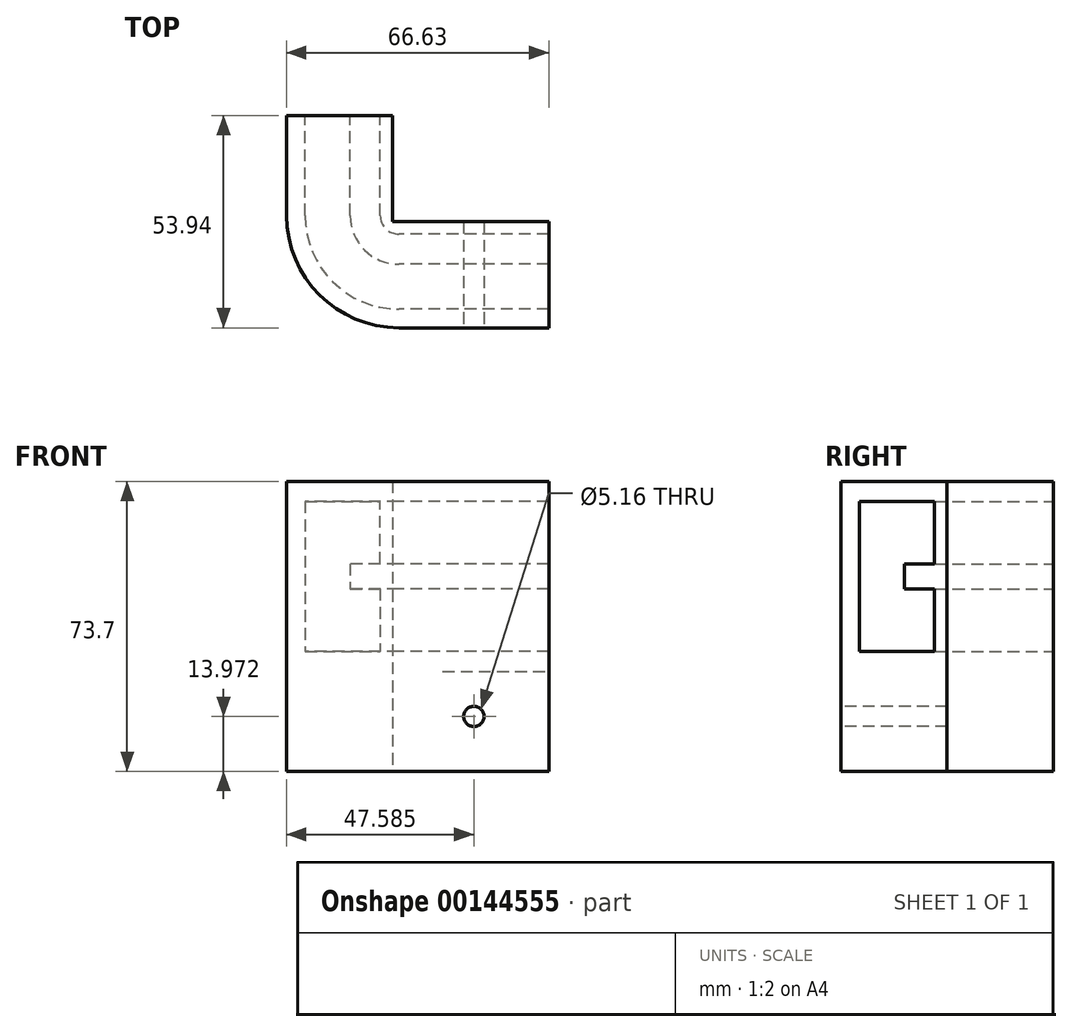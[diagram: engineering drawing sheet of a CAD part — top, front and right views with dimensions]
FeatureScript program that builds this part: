
annotation { "Feature Type Name" : "Feature", "Feature Type Description" : "" }
export const myFeature = defineFeature(function(context is Context, id is Id, definition is map)
    precondition{}
    {
        {
            var Q0;
            Q0=qCreatedBy(makeId("Front.planeOp"),FACE);
            var sketch = newSketch(context, id + "F0", { "sketchPlane" : qUnion([Q0])});
            skLineSegment(sketch, "E0.bottom", {"start": v(-12.7, 18.7) * mm, "end": v(6.35, 18.7) * mm});
            skLineSegment(sketch, "E0.top", {"start": v(-12.7, -19.4) * mm, "end": v(6.35, -19.4) * mm});
            skLineSegment(sketch, "E0.left", {"start": v(-12.7, 18.7) * mm, "end": v(-12.7, -19.4) * mm});
            skLineSegment(sketch, "E1", {"start": v(6.35, -3.53) * mm, "end": v(6.35, -19.4) * mm});
            skLineSegment(sketch, "E2", {"start": v(6.35, 2.82) * mm, "end": v(6.35, 18.7) * mm});
            skLineSegment(sketch, "E3", {"start": v(6.35, 2.82) * mm, "end": v(-1.27, 2.82) * mm});
            skLineSegment(sketch, "E4.bottom", {"start": v(-1.27, 2.82) * mm, "end": v(6.35, 2.82) * mm});
            skLineSegment(sketch, "E4.top", {"start": v(-1.27, -3.53) * mm, "end": v(6.35, -3.53) * mm});
            skLineSegment(sketch, "E4.left", {"start": v(-1.27, 2.82) * mm, "end": v(-1.27, -3.53) * mm});
            skLineSegment(sketch, "E5.bottom", {"start": v(-17.44, 23.8) * mm, "end": v(11.1, 23.8) * mm});
            skLineSegment(sketch, "E5.top", {"start": v(-17.44, -24.5) * mm, "end": v(11.1, -24.5) * mm});
            skLineSegment(sketch, "E5.left", {"start": v(-17.44, 23.8) * mm, "end": v(-17.44, -24.5) * mm});
            skLineSegment(sketch, "E5.right", {"start": v(11.1, 23.8) * mm, "end": v(11.1, -24.5) * mm});
            skLineSegment(sketch, "E6", {"start": v(-12.7, 18.7) * mm, "end": v(-17.44, 23.8) * mm, "construction": true});
            skLineSegment(sketch, "E7", {"start": v(6.35, 18.7) * mm, "end": v(11.1, 23.8) * mm, "construction": true});
            skLineSegment(sketch, "E8", {"start": v(6.35, -19.4) * mm, "end": v(11.1, -24.5) * mm, "construction": true});
            skLineSegment(sketch, "E9", {"start": v(-17.44, -24.5) * mm, "end": v(-12.7, -19.4) * mm, "construction": true});
            skSolve(sketch);
        }
        {
            var Q0;
            Q0=makeQuery(id+"F0.imprint","IMPRINT",FACE,{"disambiguationData":[TD([[makeQuery(id+"F0.imprint","IMPRINT",EDGE,{"derivedFrom":sQuery(id+"F0.wireOp",EDGE,"E0.bottom")}),1.0]])]});
            var Q1;
            Q1=sQuery(id+"F0.wireOp",EDGE,"E8");
            var Q2;
            Q2=sQuery(id+"F0.wireOp",EDGE,"E9");
            var Q3;
            Q3=sQuery(id+"F0.wireOp",EDGE,"E6");
            var Q4;
            Q4=sQuery(id+"F0.wireOp",EDGE,"E7");
            extrude(context, id + "F1", {"entities" : qUnion([Q0]), "surfaceEntities" : qUnion([Q1, Q2, Q3, Q4]), "depth" : 25.4 * mm});
        }
        {
            var Q0;
            Q0=makeQuery(id+"F1.opExtrude","CAP_FACE",FACE,{"disambiguationData":[OSD([sQuery(id+"F0.wireOp",EDGE,"E0.bottom"),sQuery(id+"F0.wireOp",EDGE,"E0.top"),sQuery(id+"F0.wireOp",EDGE,"E0.left"),sQuery(id+"F0.wireOp",EDGE,"E1"),sQuery(id+"F0.wireOp",EDGE,"E2"),sQuery(id+"F0.wireOp",EDGE,"E4.bottom"),sQuery(id+"F0.wireOp",EDGE,"E4.top"),sQuery(id+"F0.wireOp",EDGE,"E4.left"),sQuery(id+"F0.wireOp",EDGE,"E5.bottom"),sQuery(id+"F0.wireOp",EDGE,"E5.top"),sQuery(id+"F0.wireOp",EDGE,"E5.left"),sQuery(id+"F0.wireOp",EDGE,"E5.right")])],"isStart":false});
            var Q1;
            Q1=makeQuery(id+"F1.opExtrude","CAP_EDGE",EDGE,{"disambiguationData":[OSD([sQuery(id+"F0.wireOp",EDGE,"E5.right")])],"isStart":false});
            revolve(context, id + "F2", {"operationType" : NewBodyOperationType.ADD, "entities" : qUnion([Q0]), "axis" : qUnion([Q1]), "revolveType" : RevolveType.ONE_DIRECTION, "oppositeDirection" : true, "angle" : 90 * degree});
        }
        {
            var Q0;
            {var subQ0=sQuery(id+"F0.wireOp",EDGE,"E5.right");Q0=makeQuery(id+"F2.boolean.opBoolean","MERGE",FACE,{"derivedFrom":[makeQuery(id+"F1.opExtrude","SWEPT_FACE",FACE,{"disambiguationData":[OSD([subQ0])]}),makeQuery(id+"F2.opRevolve","CAP_FACE",FACE,{"disambiguationData":[OSD([sQuery(id+"F0.wireOp",EDGE,"E0.bottom"),sQuery(id+"F0.wireOp",EDGE,"E0.top"),sQuery(id+"F0.wireOp",EDGE,"E0.left"),sQuery(id+"F0.wireOp",EDGE,"E1"),sQuery(id+"F0.wireOp",EDGE,"E2"),sQuery(id+"F0.wireOp",EDGE,"E4.bottom"),sQuery(id+"F0.wireOp",EDGE,"E4.top"),sQuery(id+"F0.wireOp",EDGE,"E4.left"),sQuery(id+"F0.wireOp",EDGE,"E5.bottom"),sQuery(id+"F0.wireOp",EDGE,"E5.top"),sQuery(id+"F0.wireOp",EDGE,"E5.left"),subQ0])],"isStart":false})]});}
            extrude(context, id + "F3", {"entities" : qUnion([Q0]), "operationType" : NewBodyOperationType.ADD, "depth" : 38.1 * mm, "offsetDistance" : 25.4 * mm});
        }
        {
            var Q0;
            {var subQ0=sQuery(id+"F0.wireOp",EDGE,"E5.top");Q0=makeQuery(id+"F3.boolean.opBoolean","MERGE",FACE,{"derivedFrom":[makeQuery(id+"F2.boolean.opBoolean","MERGE",FACE,{"derivedFrom":[makeQuery(id+"F1.opExtrude","SWEPT_FACE",FACE,{"disambiguationData":[OSD([subQ0])]}),makeQuery(id+"F2.opRevolve","SWEPT_FACE",FACE,{"disambiguationData":[OSD([subQ0])]})]}),makeQuery(id+"F3.opExtrude","SWEPT_FACE",FACE,{"disambiguationData":[OSD([subQ0,sQuery(id+"F0.wireOp",EDGE,"E5.right")])]})]});}
            var sketch = newSketch(context, id + "F4", { "sketchPlane" : qUnion([Q0])});
            skLineSegment(sketch, "E10.bottom", {"start": v(22.23, 0) * mm, "end": v(49.2, 0) * mm});
            skLineSegment(sketch, "E10.top", {"start": v(22.23, 26.97) * mm, "end": v(49.2, 26.97) * mm});
            skLineSegment(sketch, "E10.left", {"start": v(22.23, 0) * mm, "end": v(22.23, 26.97) * mm});
            skLineSegment(sketch, "E10.right", {"start": v(49.2, 0) * mm, "end": v(49.2, 26.97) * mm});
            skSolve(sketch);
        }
        {
            var Q0;
            Q0 = qSketchRegion(id + "F4", true);
            extrude(context, id + "F5", {"entities" : qUnion([Q0]), "operationType" : NewBodyOperationType.REMOVE, "endBound" : BoundingType.SYMMETRIC, "oppositeDirection" : true, "depth" : 100.3 * mm});
        }
        {
            var Q0;
            {var subQ0=sQuery(id+"F0.wireOp",EDGE,"E5.top");Q0=makeQuery(id+"F3.boolean.opBoolean","MERGE",FACE,{"derivedFrom":[makeQuery(id+"F2.boolean.opBoolean","MERGE",FACE,{"derivedFrom":[makeQuery(id+"F1.opExtrude","SWEPT_FACE",FACE,{"disambiguationData":[OSD([subQ0])]}),makeQuery(id+"F2.opRevolve","SWEPT_FACE",FACE,{"disambiguationData":[OSD([subQ0])]})]}),makeQuery(id+"F3.opExtrude","SWEPT_FACE",FACE,{"disambiguationData":[OSD([subQ0,sQuery(id+"F0.wireOp",EDGE,"E5.right")])]})]});}
            var sketch = newSketch(context, id + "F6", { "sketchPlane" : qUnion([Q0])});
            skLineSegment(sketch, "E11.bottom", {"start": v(22.23, 26.97) * mm, "end": v(49.2, 27) * mm});
            skLineSegment(sketch, "E11.top", {"start": v(22.22, 33.32) * mm, "end": v(49.2, 33.34) * mm});
            skLineSegment(sketch, "E11.left", {"start": v(22.23, 26.97) * mm, "end": v(22.22, 33.32) * mm});
            skLineSegment(sketch, "E11.right", {"start": v(49.2, 27) * mm, "end": v(49.2, 33.34) * mm});
            skPoint(sketch, "E12.oppositeSnap0", {"position": v(22.22, 30.14) * mm});
            skLineSegment(sketch, "E12.bottom", {"start": v(49.2, 53.94) * mm, "end": v(22.22, 53.94) * mm});
            skLineSegment(sketch, "E12.top", {"start": v(49.2, 47.59) * mm, "end": v(22.22, 47.59) * mm});
            skLineSegment(sketch, "E12.left", {"start": v(49.2, 53.94) * mm, "end": v(49.2, 47.59) * mm});
            skLineSegment(sketch, "E12.right", {"start": v(22.22, 53.94) * mm, "end": v(22.22, 47.59) * mm});
            skSolve(sketch);
        }
        {
            var Q0;
            {var subQ7=sQuery(id+"F6.wireOp",EDGE,"E11.top");Q0=makeQuery(id+"F6.imprint","IMPRINT",FACE,{"disambiguationData":[TD([[makeQuery(id+"F6.imprint","IMPRINT",EDGE,{"derivedFrom":subQ7}),-1.0]])]});}
            var Q1;
            {var subQ1=sQuery(id+"F6.wireOp",EDGE,"E12.top");Q1=makeQuery(id+"F6.imprint","IMPRINT",FACE,{"disambiguationData":[TD([[makeQuery(id+"F6.imprint","IMPRINT",EDGE,{"derivedFrom":subQ1}),-1.0]])]});}
            var Q2;
            {var subQ7=sQuery(id+"F6.wireOp",EDGE,"E11.top");Q2=makeQuery(id+"F6.imprint","IMPRINT",FACE,{"disambiguationData":[TD([[makeQuery(id+"F6.imprint","IMPRINT",EDGE,{"derivedFrom":subQ7}),1.0]])]});}
            extrude(context, id + "F7", {"entities" : qUnion([Q0, Q1, Q2]), "operationType" : NewBodyOperationType.ADD, "depth" : 25.4 * mm});
        }
        {
            var Q0;
            Q0=makeQuery(id+"F7.boolean.opBoolean","MERGE",FACE,{"derivedFrom":[makeQuery(id+"F3.opExtrude","SWEPT_FACE",FACE,{"disambiguationData":[OSD([sQuery(id+"F0.wireOp",EDGE,"E5.left")])]}),makeQuery(id+"F7.opExtrude","SWEPT_FACE",FACE,{"disambiguationData":[OSD([sQuery(id+"F6.wireOp",EDGE,"E12.bottom")])]})]});
            var sketch = newSketch(context, id + "F8", { "sketchPlane" : qUnion([Q0])});
            skCircle(sketch, "E13", {"center": v(30.14, -35.93) * mm, "radius": 2.58 * mm});
            skLineSegment(sketch, "E14", {"start": v(30.14, -35.93) * mm, "end": v(49.2, -35.93) * mm});
            skLineSegment(sketch, "E15", {"start": v(30.14, -35.93) * mm, "end": v(11.1, -35.93) * mm});
            skCircle(sketch, "E16", {"center": v(30.14, -35.93) * mm, "radius": 14.27 * mm});
            skSolve(sketch);
        }
        {
            var Q0;
            {var subQ0=sQuery(id+"F8.wireOp",EDGE,"E14");var subQ1=sQuery(id+"F8.wireOp",EDGE,"E13");var subQ2=makeQuery(id+"F8.imprint","INTERSECT",VERTEX,{"derivedFrom":[subQ1,subQ0]});Q0=makeQuery(id+"F8.imprint","IMPRINT",FACE,{"disambiguationData":[TD([[makeQuery(id+"F8.imprint","IMPRINT",EDGE,{"disambiguationData":[TD([[subQ2,1.0]])],"derivedFrom":subQ1}),1.0]])]});}
            var Q1;
            {var subQ0=sQuery(id+"F8.wireOp",EDGE,"E14");var subQ1=sQuery(id+"F8.wireOp",EDGE,"E13");var subQ2=makeQuery(id+"F8.imprint","INTERSECT",VERTEX,{"derivedFrom":[subQ1,subQ0]});Q1=makeQuery(id+"F8.imprint","IMPRINT",FACE,{"disambiguationData":[TD([[makeQuery(id+"F8.imprint","IMPRINT",EDGE,{"disambiguationData":[TD([[subQ2,-1.0]])],"derivedFrom":subQ1}),1.0]])]});}
            var Q2;
            Q2=sQuery(id+"F8.wireOp",EDGE,"E13");
            extrude(context, id + "F9", {"entities" : qUnion([Q0, Q1]), "operationType" : NewBodyOperationType.REMOVE, "surfaceEntities" : qUnion([Q2]), "oppositeDirection" : true, "depth" : 38.1 * mm});
        }
        {
            var Q0;
            Q0=makeQuery(id+"F7.boolean.opBoolean","MERGE",FACE,{"derivedFrom":[makeQuery(id+"F3.opExtrude","SWEPT_FACE",FACE,{"disambiguationData":[OSD([sQuery(id+"F0.wireOp",EDGE,"E5.left")])]}),makeQuery(id+"F7.opExtrude","SWEPT_FACE",FACE,{"disambiguationData":[OSD([sQuery(id+"F6.wireOp",EDGE,"E12.bottom")])]})]});
            var sketch = newSketch(context, id + "F10", { "sketchPlane" : qUnion([Q0])});
            skSolve(sketch);
        }
        {
            var Q0;
            {var subQ0=sQuery(id+"F4.wireOp",EDGE,"E10.left");Q0=makeQuery(id+"F7.boolean.opBoolean","MERGE",FACE,{"derivedFrom":[makeQuery(id+"F5.boolean.opBoolean","COPY",FACE,{"derivedFrom":makeQuery(id+"F5.opExtrude","SWEPT_FACE",FACE,{"disambiguationData":[OSD([subQ0])]})}),makeQuery(id+"F7.opExtrude","SWEPT_FACE",FACE,{"disambiguationData":[OSD([sQuery(id+"F0.wireOp",EDGE,"E5.top"),sQuery(id+"F0.wireOp",EDGE,"E5.right"),subQ0])]})]});}
            extrude(context, id + "F11", {"entities" : qUnion([Q0]), "operationType" : NewBodyOperationType.REMOVE, "oppositeDirection" : true, "depth" : 12.7 * mm, "offsetDistance" : 25.4 * mm});
        }
    });
